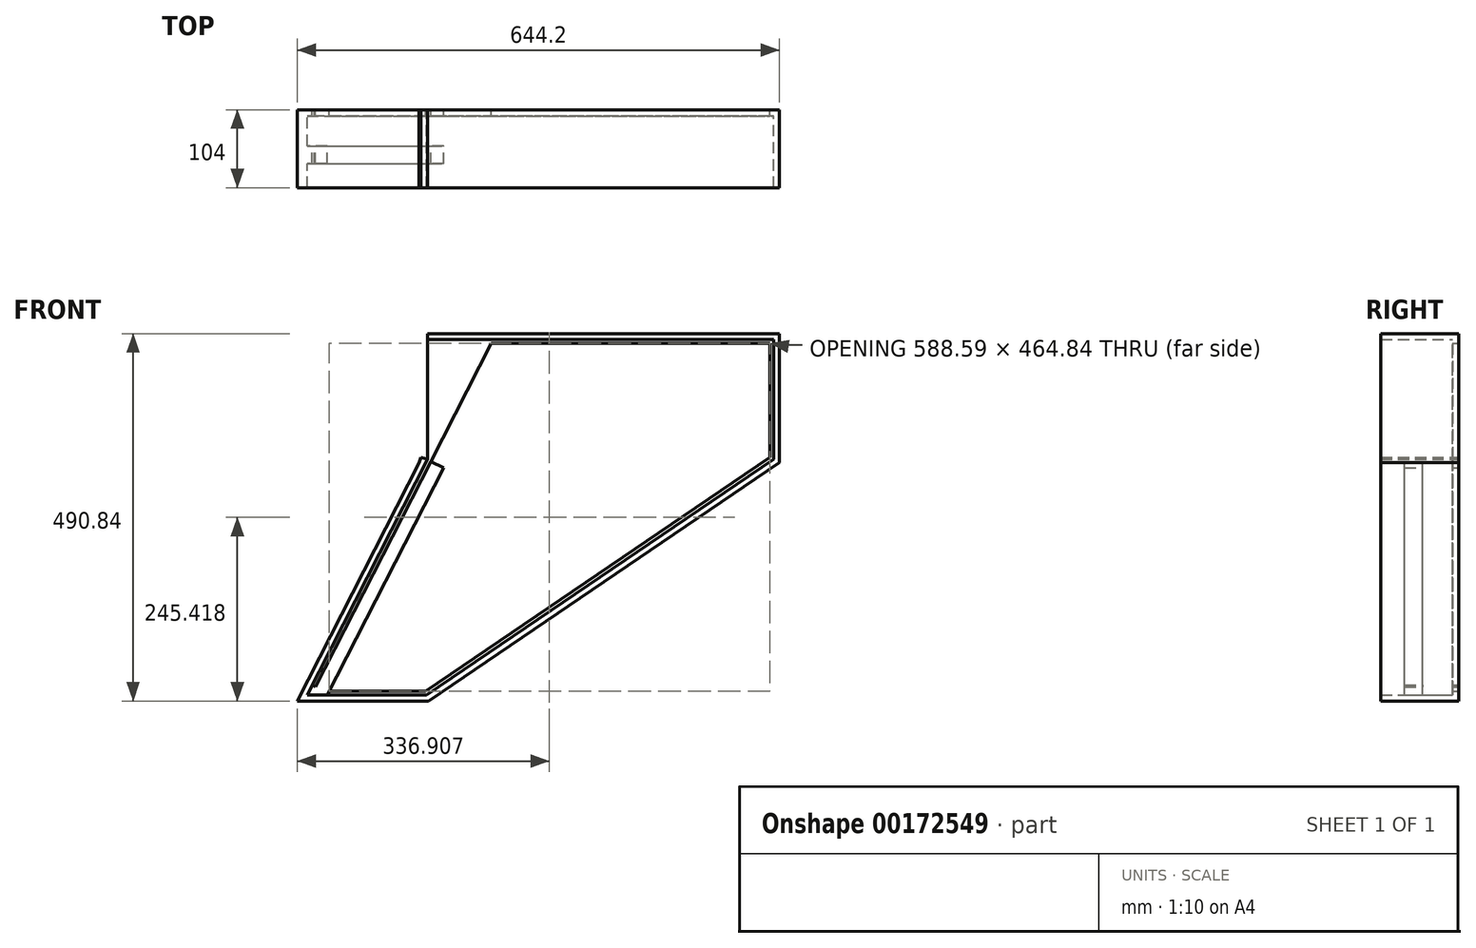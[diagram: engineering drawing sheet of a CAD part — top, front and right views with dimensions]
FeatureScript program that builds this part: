
annotation { "Feature Type Name" : "Feature", "Feature Type Description" : "" }
export const myFeature = defineFeature(function(context is Context, id is Id, definition is map)
    precondition{}
    {
        {
            assignVariable(context, id + "F0", {"name" : "multiplier", "anyValue" : 8});
        }
        {
            assignVariable(context, id + "F1", {"name" : "L8", "anyValue" : 3 * (getVariable(context, 'multiplier'))});
        }
        {
            assignVariable(context, id + "F2", {"name" : "W1", "anyValue" : 1 * (getVariable(context, 'multiplier'))});
        }
        {
            assignVariable(context, id + "F3", {"name" : "W2", "anyValue" : 13 * (getVariable(context, 'multiplier'))});
        }
        {
            assignVariable(context, id + "F4", {"name" : "W3", "anyValue" : getVariable(context, 'L8')});
        }
        {
            var Q0;
            Q0=qCreatedBy(makeId("Front.planeOp"),FACE);
            var sketch = newSketch(context, id + "F5", { "sketchPlane" : qUnion([Q0])});
            skLineSegment(sketch, "E0", {"start": v(0, 0) * mm, "end": v(720, 0) * mm});
            skLineSegment(sketch, "E1", {"start": v(720, 0) * mm, "end": v(720, -160) * mm});
            skLineSegment(sketch, "E2", {"start": v(720, -160) * mm, "end": v(256.89, -474.84) * mm});
            skLineSegment(sketch, "E3", {"start": v(256.89, -474.84) * mm, "end": v(96.89, -474.84) * mm});
            skLineSegment(sketch, "E4", {"start": v(96.89, -474.84) * mm, "end": v(258.15, -160) * mm});
            skLineSegment(sketch, "E5", {"start": v(258.15, -160) * mm, "end": v(0, -80) * mm});
            skLineSegment(sketch, "E6", {"start": v(0, -80) * mm, "end": v(0, 0) * mm});
            skLineSegment(sketch, "E7.0", {"start": v(105.07, -469.84) * mm, "end": v(343.16, -5) * mm});
            skLineSegment(sketch, "E7.2", {"start": v(715, -5) * mm, "end": v(715, -157.35) * mm});
            skLineSegment(sketch, "E7.3", {"start": v(715, -157.35) * mm, "end": v(255.35, -469.84) * mm});
            skLineSegment(sketch, "E7.4", {"start": v(255.35, -469.84) * mm, "end": v(105.07, -469.84) * mm});
            skLineSegment(sketch, "E8", {"start": v(343.16, -5) * mm, "end": v(715, -5) * mm});
            skLineSegment(sketch, "E9", {"start": v(258.15, -160) * mm, "end": v(258.15, 0) * mm});
            skLineSegment(sketch, "E10.0", {"start": v(-8, -85.9) * mm, "end": v(-8, 8) * mm});
            skLineSegment(sketch, "E10.1", {"start": v(246.7, -164.82) * mm, "end": v(-8, -85.9) * mm});
            skLineSegment(sketch, "E10.2", {"start": v(728, 8) * mm, "end": v(728, -164.23) * mm});
            skLineSegment(sketch, "E10.3", {"start": v(728, -164.23) * mm, "end": v(259.35, -482.84) * mm});
            skLineSegment(sketch, "E10.4", {"start": v(259.35, -482.84) * mm, "end": v(83.8, -482.84) * mm});
            skLineSegment(sketch, "E10.5", {"start": v(-8, 8) * mm, "end": v(728, 8) * mm});
            skLineSegment(sketch, "E10.6", {"start": v(83.8, -482.84) * mm, "end": v(246.7, -164.82) * mm});
            skLineSegment(sketch, "E11", {"start": v(246.7, -164.82) * mm, "end": v(249.06, -157.18) * mm});
            skLineSegment(sketch, "E12", {"start": v(258.15, 0) * mm, "end": v(258.15, 8) * mm});
            skLineSegment(sketch, "E13.0", {"start": v(123.85, -474.84) * mm, "end": v(279.31, -171.33) * mm});
            skLineSegment(sketch, "E14", {"start": v(279.31, -171.33) * mm, "end": v(257.95, -160.4) * mm});
            skLineSegment(sketch, "E15", {"start": v(103.86, -461.23) * mm, "end": v(108.31, -463.5) * mm});
            skLineSegment(sketch, "E16", {"start": v(108.31, -463.5) * mm, "end": v(103.72, -461.5) * mm});
            skLineSegment(sketch, "E17", {"start": v(103.72, -461.5) * mm, "end": v(108.28, -463.57) * mm});
            skLineSegment(sketch, "E18", {"start": v(108.28, -463.57) * mm, "end": v(103.74, -461.47) * mm});
            skLineSegment(sketch, "E19", {"start": v(103.81, -461.32) * mm, "end": v(108.22, -463.68) * mm});
            skLineSegment(sketch, "E20", {"start": v(258.15, -160) * mm, "end": v(262.6, -162.28) * mm});
            skSolve(sketch);
        }
        {
            var Q0;
            {var subQ7=sQuery(id+"F5.wireOp",EDGE,"E1");Q0=makeQuery(id+"F5.imprint","IMPRINT",FACE,{"disambiguationData":[TD([[makeQuery(id+"F5.imprint","IMPRINT",EDGE,{"derivedFrom":subQ7}),1.0]])]});}
            var Q1;
            {var subQ0=sQuery(id+"F5.wireOp",EDGE,"E1");Q1=makeQuery(id+"F5.imprint","IMPRINT",FACE,{"disambiguationData":[TD([[makeQuery(id+"F5.imprint","IMPRINT",EDGE,{"derivedFrom":subQ0}),-1.0]])]});}
            var Q2;
            {var subQ3=sQuery(id+"F5.wireOp",EDGE,"E13.0");Q2=makeQuery(id+"F5.imprint","IMPRINT",FACE,{"disambiguationData":[TD([[makeQuery(id+"F5.imprint","IMPRINT",EDGE,{"derivedFrom":subQ3}),1.0]])]});}
            var Q3;
            {var subQ5=sQuery(id+"F5.wireOp",EDGE,"E4");var subQ6=sQuery(id+"F5.wireOp",EDGE,"E3");var subQ7=makeQuery(id+"F5.imprint","INTERSECT",VERTEX,{"derivedFrom":[subQ6,subQ5]});Q3=makeQuery(id+"F5.imprint","IMPRINT",FACE,{"disambiguationData":[TD([[makeQuery(id+"F5.imprint","IMPRINT",EDGE,{"disambiguationData":[TD([[subQ7,1.0]])],"derivedFrom":subQ6}),-1.0]])]});}
            var Q4;
            {var subQ0=sQuery(id+"F5.wireOp",EDGE,"E20");Q4=makeQuery(id+"F5.imprint","IMPRINT",FACE,{"disambiguationData":[TD([[makeQuery(id+"F5.imprint","IMPRINT",EDGE,{"derivedFrom":subQ0}),-1.0]])]});}
            var Q5;
            {var subQ3=sQuery(id+"F5.wireOp",EDGE,"E15");Q5=makeQuery(id+"F5.imprint","IMPRINT",FACE,{"disambiguationData":[TD([[makeQuery(id+"F5.imprint","IMPRINT",EDGE,{"derivedFrom":subQ3}),1.0]])]});}
            extrude(context, id + "F6", {"entities" : qUnion([Q0, Q1, Q2, Q3, Q4, Q5]), "depth" : (getVariable(context, 'W1')) * mm});
        }
        {
            var Q0;
            {var subQ7=sQuery(id+"F5.wireOp",EDGE,"E1");Q0=makeQuery(id+"F5.imprint","IMPRINT",FACE,{"disambiguationData":[TD([[makeQuery(id+"F5.imprint","IMPRINT",EDGE,{"derivedFrom":subQ7}),1.0]])]});}
            extrude(context, id + "F7", {"entities" : qUnion([Q0]), "operationType" : NewBodyOperationType.ADD, "depth" : (getVariable(context, 'W2')) * mm});
        }
        {
            var Q0;
            {var subQ3=sQuery(id+"F5.wireOp",EDGE,"E13.0");Q0=makeQuery(id+"F5.imprint","IMPRINT",FACE,{"disambiguationData":[TD([[makeQuery(id+"F5.imprint","IMPRINT",EDGE,{"derivedFrom":subQ3}),1.0]])]});}
            extrude(context, id + "F8", {"entities" : qUnion([Q0]), "operationType" : NewBodyOperationType.ADD, "depth" : ((getVariable(context, 'W2') + getVariable(context, 'W3')) / 2 + getVariable(context, 'W1')) * mm, "hasSecondDirection" : true, "secondDirectionOppositeDirection" : false, "secondDirectionDepth" : ((getVariable(context, 'W2') - getVariable(context, 'W3')) / 2 + getVariable(context, 'W1')) * mm});
        }
    });
